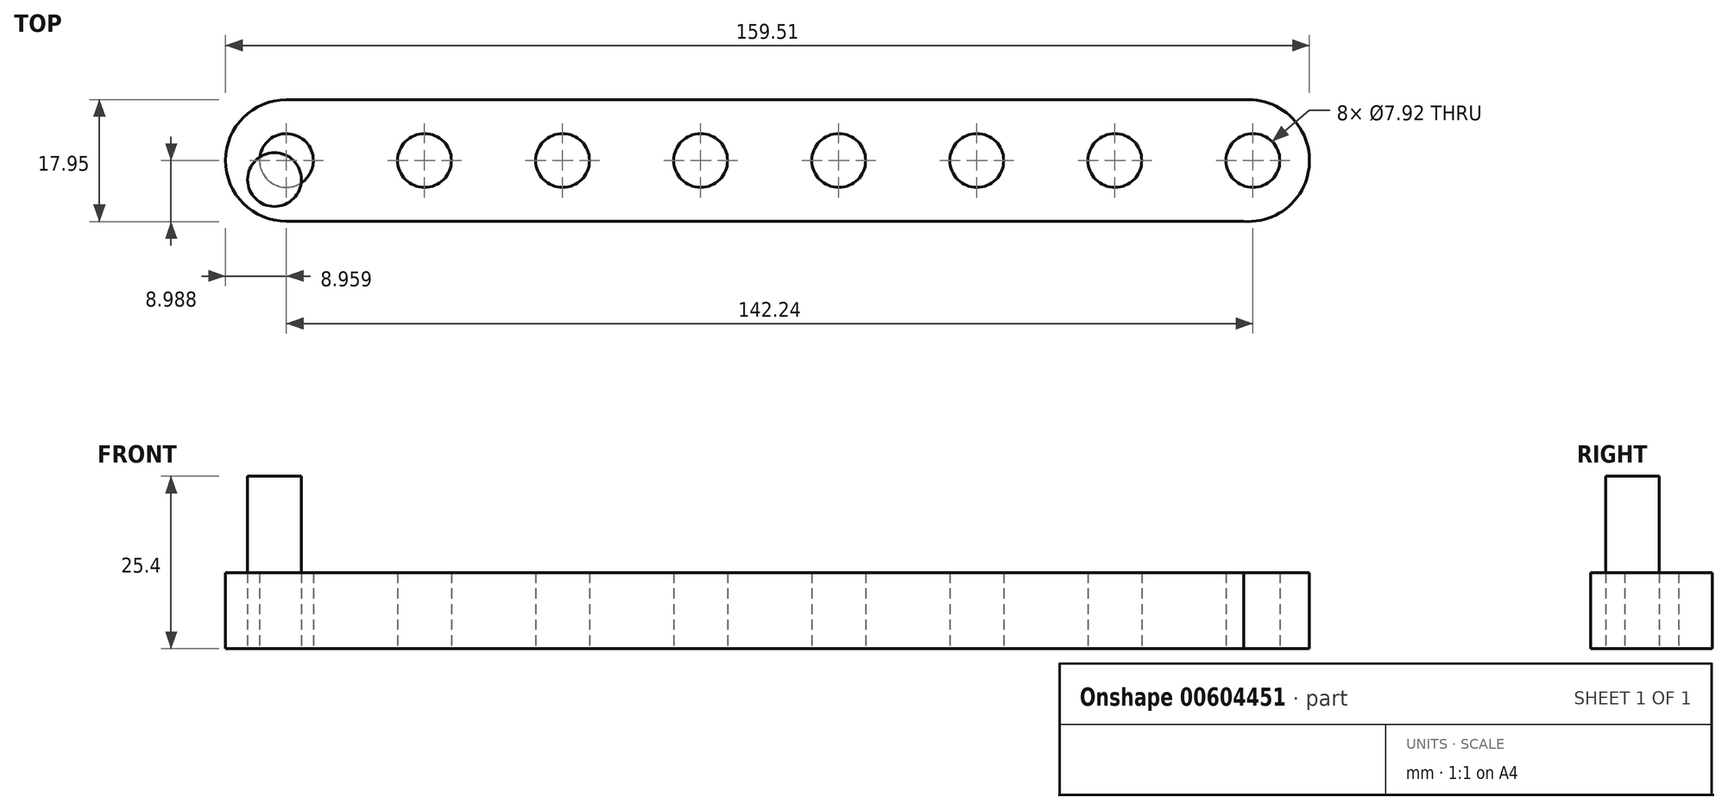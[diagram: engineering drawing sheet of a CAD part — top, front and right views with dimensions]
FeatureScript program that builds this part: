
annotation { "Feature Type Name" : "Feature", "Feature Type Description" : "" }
export const myFeature = defineFeature(function(context is Context, id is Id, definition is map)
    precondition{}
    {
        {
            var Q0;
            Q0=qCreatedBy(makeId("Top.planeOp"),FACE);
            var sketch = newSketch(context, id + "F0", { "sketchPlane" : qUnion([Q0])});
            skLineSegment(sketch, "E0", {"start": v(-65.1, 0) * mm, "end": v(75.8, 0) * mm});
            skLineSegment(sketch, "E1", {"start": v(-65.1, 17.92) * mm, "end": v(76.5, 17.92) * mm});
            skArc(sketch, "E2", {"start": v(-65.1, 17.92) * mm, "mid": v(-74.05, 8.96) * mm, "end": v(-65.1, 0) * mm});
            skArc(sketch, "E3", {"start": v(75.8, 0) * mm, "mid": v(85.46, 8.6) * mm, "end": v(76.5, 17.92) * mm});
            skSolve(sketch);
        }
        {
            var Q0;
            Q0=makeQuery(id+"F0.imprint","IMPRINT",FACE,{"disambiguationData":[TD([[makeQuery(id+"F0.imprint","IMPRINT",EDGE,{"derivedFrom":sQuery(id+"F0.wireOp",EDGE,"E0")}),1.0]])]});
            extrude(context, id + "F1", {"entities" : qUnion([Q0]), "depth" : 11.18 * mm, "offsetDistance" : 25.4 * mm});
        }
        {
            var Q0;
            Q0=makeQuery(id+"F1.opExtrude","CAP_FACE",FACE,{"disambiguationData":[OSD([sQuery(id+"F0.wireOp",EDGE,"E0"),sQuery(id+"F0.wireOp",EDGE,"E1"),sQuery(id+"F0.wireOp",EDGE,"E2"),sQuery(id+"F0.wireOp",EDGE,"E3")])],"isStart":true});
            var sketch = newSketch(context, id + "F2", { "sketchPlane" : qUnion([Q0])});
            skCircle(sketch, "E4", {"center": v(-65.1, -8.96) * mm, "radius": 3.96 * mm});
            skCircle(sketch, "E5.1.0.0", {"center": v(-44.77, -8.96) * mm, "radius": 3.96 * mm});
            skCircle(sketch, "E5.2.0.0", {"center": v(-24.45, -8.96) * mm, "radius": 3.96 * mm});
            skLineSegment(sketch, "E5.direction1", {"start": v(-65.1, -8.96) * mm, "end": v(-44.77, -8.96) * mm, "construction": true});
            skCircle(sketch, "E6.0.3.0", {"center": v(-4.13, -8.96) * mm, "radius": 3.96 * mm});
            skCircle(sketch, "E6.0.4.0", {"center": v(16.19, -8.96) * mm, "radius": 3.96 * mm});
            skCircle(sketch, "E6.0.5.0", {"center": v(36.5, -8.96) * mm, "radius": 3.96 * mm});
            skCircle(sketch, "E6.0.6.0", {"center": v(56.83, -8.96) * mm, "radius": 3.96 * mm});
            skCircle(sketch, "E6.0.7.0", {"center": v(77.15, -8.96) * mm, "radius": 3.96 * mm});
            skSolve(sketch);
        }
        {
            var Q0;
            Q0=makeQuery(id+"F2.imprint","IMPRINT",FACE,{"disambiguationData":[TD([[makeQuery(id+"F2.imprint","IMPRINT",EDGE,{"derivedFrom":sQuery(id+"F2.wireOp",EDGE,"E5.2.0.0")}),1.0]])]});
            var Q1;
            Q1=makeQuery(id+"F2.imprint","IMPRINT",FACE,{"disambiguationData":[TD([[makeQuery(id+"F2.imprint","IMPRINT",EDGE,{"derivedFrom":sQuery(id+"F2.wireOp",EDGE,"E6.0.3.0")}),1.0]])]});
            var Q2;
            Q2=makeQuery(id+"F2.imprint","IMPRINT",FACE,{"disambiguationData":[TD([[makeQuery(id+"F2.imprint","IMPRINT",EDGE,{"derivedFrom":sQuery(id+"F2.wireOp",EDGE,"E6.0.4.0")}),1.0]])]});
            var Q3;
            Q3=makeQuery(id+"F2.imprint","IMPRINT",FACE,{"disambiguationData":[TD([[makeQuery(id+"F2.imprint","IMPRINT",EDGE,{"derivedFrom":sQuery(id+"F2.wireOp",EDGE,"E6.0.5.0")}),1.0]])]});
            var Q4;
            Q4=makeQuery(id+"F2.imprint","IMPRINT",FACE,{"disambiguationData":[TD([[makeQuery(id+"F2.imprint","IMPRINT",EDGE,{"derivedFrom":sQuery(id+"F2.wireOp",EDGE,"E6.0.6.0")}),1.0]])]});
            var Q5;
            Q5=makeQuery(id+"F2.imprint","IMPRINT",FACE,{"disambiguationData":[TD([[makeQuery(id+"F2.imprint","IMPRINT",EDGE,{"derivedFrom":sQuery(id+"F2.wireOp",EDGE,"E6.0.7.0")}),1.0]])]});
            var Q6;
            Q6=makeQuery(id+"F2.imprint","IMPRINT",FACE,{"disambiguationData":[TD([[makeQuery(id+"F2.imprint","IMPRINT",EDGE,{"derivedFrom":sQuery(id+"F2.wireOp",EDGE,"E5.1.0.0")}),1.0]])]});
            var Q7;
            Q7=makeQuery(id+"F2.imprint","IMPRINT",FACE,{"disambiguationData":[TD([[makeQuery(id+"F2.imprint","IMPRINT",EDGE,{"derivedFrom":sQuery(id+"F2.wireOp",EDGE,"E4")}),1.0]])]});
            extrude(context, id + "F3", {"entities" : qUnion([Q0, Q1, Q2, Q3, Q4, Q5, Q6, Q7]), "operationType" : NewBodyOperationType.REMOVE, "oppositeDirection" : true, "depth" : 25.4 * mm, "offsetDistance" : 25.4 * mm});
        }
        {
            var Q0;
            Q0=qCreatedBy(makeId("Top.planeOp"),FACE);
            var sketch = newSketch(context, id + "F4", { "sketchPlane" : qUnion([Q0])});
            skCircle(sketch, "E7", {"center": v(-66.86, 6.15) * mm, "radius": 3.96 * mm});
            skSolve(sketch);
        }
        {
            var Q0;
            Q0=makeQuery(id+"F4.imprint","IMPRINT",FACE,{"disambiguationData":[TD([[makeQuery(id+"F4.imprint","IMPRINT",EDGE,{"derivedFrom":sQuery(id+"F4.wireOp",EDGE,"E7")}),1.0]])]});
            extrude(context, id + "F5", {"entities" : qUnion([Q0]), "depth" : 25.4 * mm, "offsetDistance" : 25.4 * mm});
        }
    });
